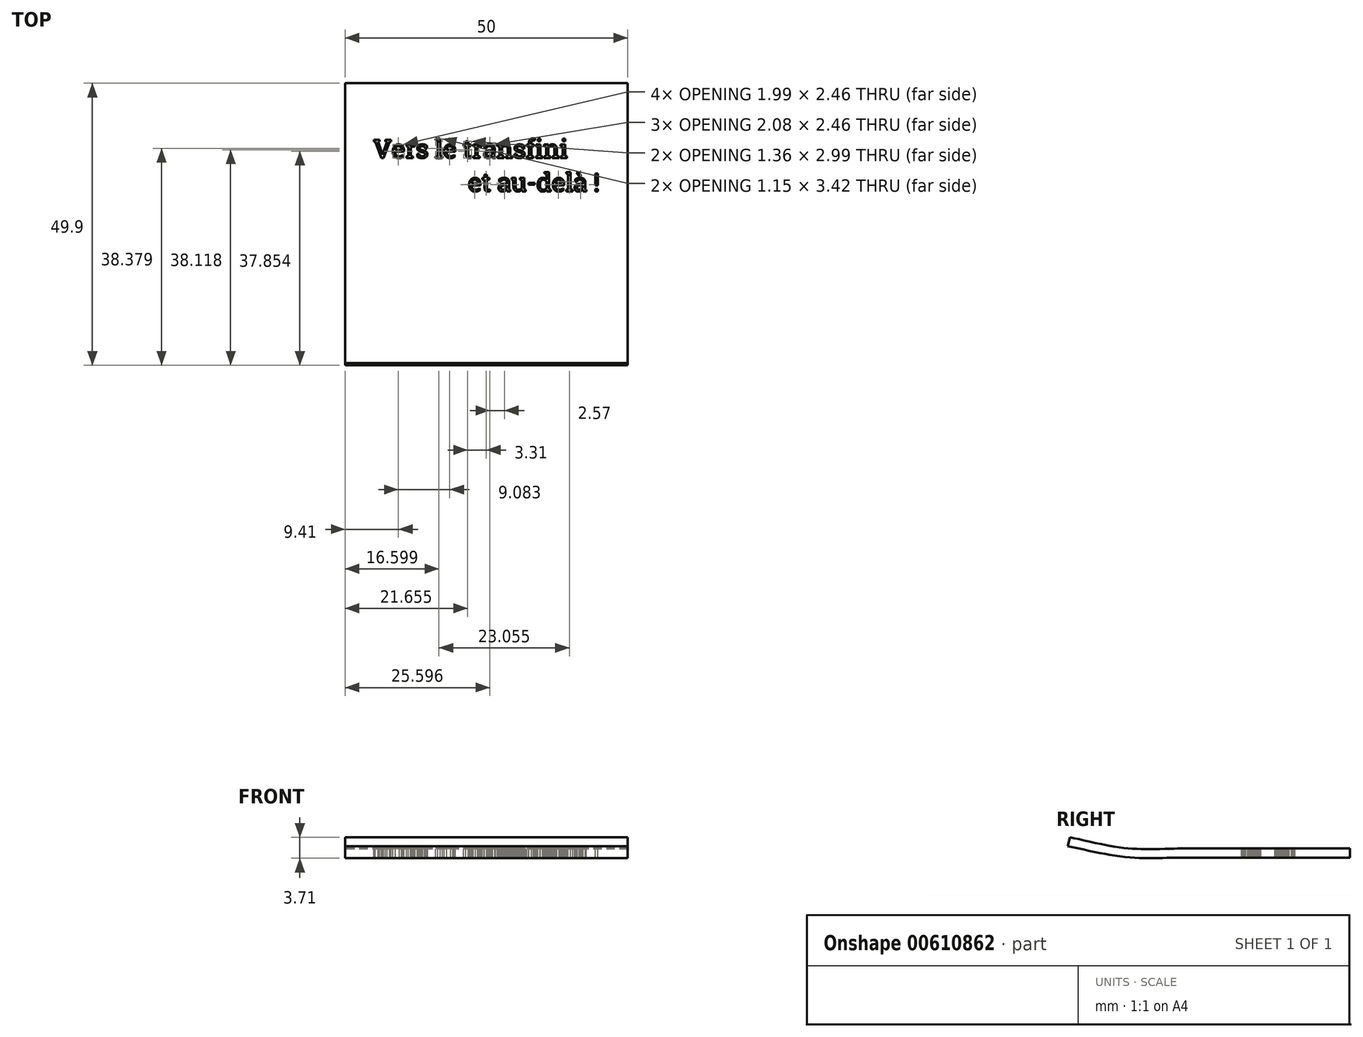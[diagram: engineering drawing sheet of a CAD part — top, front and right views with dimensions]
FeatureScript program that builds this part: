
annotation { "Feature Type Name" : "Feature", "Feature Type Description" : "" }
export const myFeature = defineFeature(function(context is Context, id is Id, definition is map)
    precondition{}
    {
        {
            var Q0;
            Q0=qCreatedBy(makeId("Right.planeOp"),FACE);
            var sketch = newSketch(context, id + "F0", { "sketchPlane" : qUnion([Q0])});
            skLineSegment(sketch, "E0", {"start": v(0, 0) * mm, "end": v(-30, 0) * mm});
            skPoint(sketch, "E1.endDerivative.orphan", {"position": v(-49.9, 2.04) * mm});
            skFitSpline(sketch, "E2", {"points": [v(-30, 0) * mm, v(-38.7, 0) * mm, v(-49.9, 2.04) * mm], "startDerivative": vector(-18.12, 0) * mm, "endDerivative": vector(-21.61, 4.84) * mm});
            skFitSpline(sketch, "E3.0", {"points": [v(-30, 1.6) * mm, v(-30.78, 1.6) * mm, v(-32.32, 1.56) * mm, v(-34.6, 1.5) * mm, v(-36.5, 1.49) * mm, v(-38.03, 1.55) * mm, v(-39.6, 1.67) * mm, v(-41.64, 1.95) * mm, v(-45.05, 2.58) * mm, v(-47.74, 3.2) * mm, v(-49.55, 3.6) * mm]});
            skLineSegment(sketch, "E3.1", {"start": v(0, 1.6) * mm, "end": v(-30, 1.6) * mm});
            skLineSegment(sketch, "E4", {"start": v(-49.55, 3.6) * mm, "end": v(-49.9, 2.04) * mm});
            skLineSegment(sketch, "E5", {"start": v(0, 1.6) * mm, "end": v(0, 0) * mm});
            skSolve(sketch);
        }
        {
            var Q0;
            Q0=makeQuery(id+"F0.imprint","IMPRINT",FACE,{"disambiguationData":[TD([[makeQuery(id+"F0.imprint","IMPRINT",EDGE,{"derivedFrom":sQuery(id+"F0.wireOp",EDGE,"E0")}),-1.0]])]});
            extrude(context, id + "F1", {"entities" : qUnion([Q0]), "depth" : 50 * mm, "offsetDistance" : 25 * mm});
        }
        {
            var Q0;
            Q0=makeQuery(id+"F1.opExtrude","SWEPT_FACE",FACE,{"disambiguationData":[OSD([sQuery(id+"F0.wireOp",EDGE,"E3.1")])]});
            var sketch = newSketch(context, id + "F2", { "sketchPlane" : qUnion([Q0])});
            skText(sketch, "E6", { "text": "Vers le transfini \n               et au-delà !", "fontName": "RobotoSlab-Regular.ttf"});
            const initialGuessF2  = {"E6": [0.005, -0.01323, 1, 0, 0.00323]};
            skSetInitialGuess(sketch, initialGuessF2);
            skSolve(sketch);
        }
        {
            var Q0;
            Q0=qSketchRegion(id+"F2",true);
            extrude(context, id + "F3", {"entities" : qUnion([Q0]), "operationType" : NewBodyOperationType.REMOVE, "oppositeDirection" : true, "depth" : 1.6 * mm, "offsetDistance" : 25 * mm});
        }
    });
